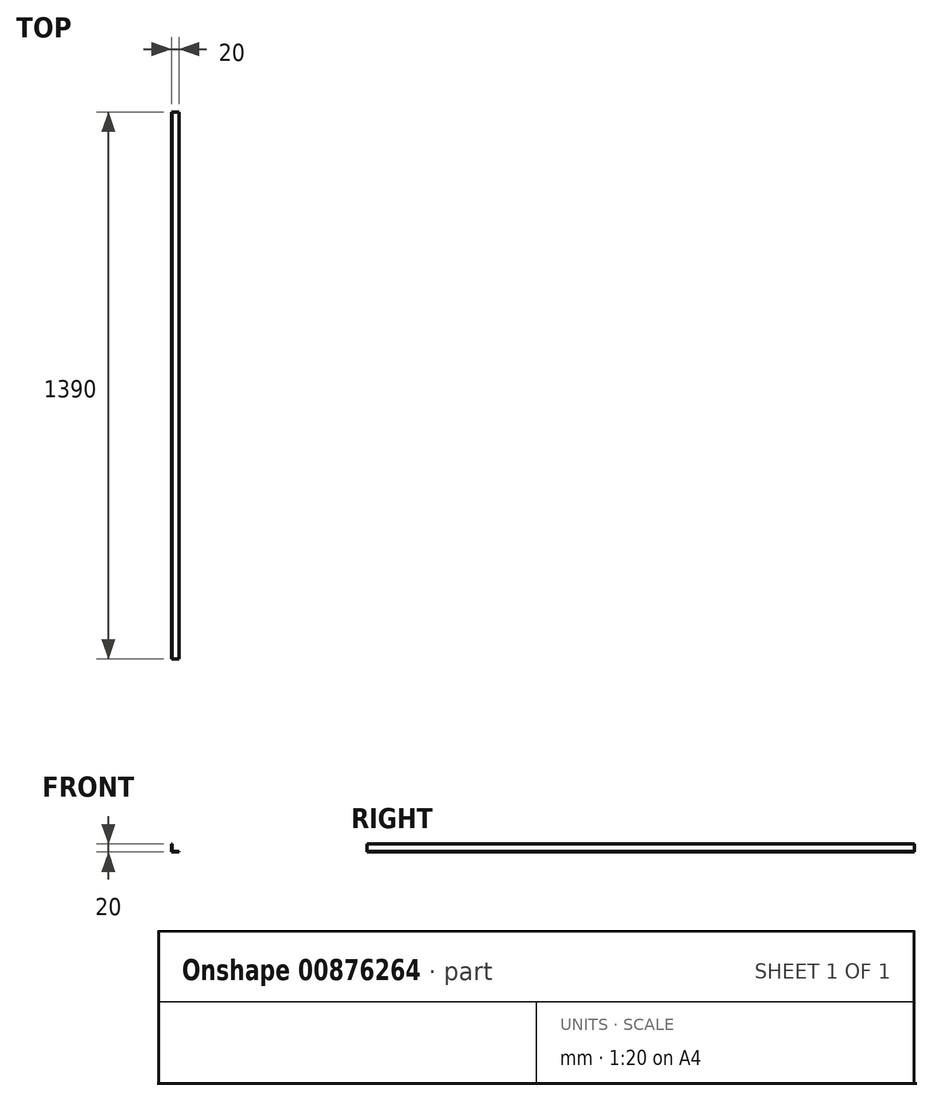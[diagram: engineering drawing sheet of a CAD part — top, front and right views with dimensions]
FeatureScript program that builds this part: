
annotation { "Feature Type Name" : "Feature", "Feature Type Description" : "" }
export const myFeature = defineFeature(function(context is Context, id is Id, definition is map)
    precondition{}
    {
        {
            var Q0;
            Q0=qCreatedBy(makeId("Front.planeOp"),FACE);
            var sketch = newSketch(context, id + "F0", { "sketchPlane" : qUnion([Q0])});
            skLineSegment(sketch, "E0", {"start": v(20, -29.07) * mm, "end": v(20, -27.57) * mm});
            skLineSegment(sketch, "E1", {"start": v(1.5, -9.07) * mm, "end": v(0, -9.07) * mm});
            skLineSegment(sketch, "E2", {"start": v(20, -29.07) * mm, "end": v(0, -29.07) * mm});
            skLineSegment(sketch, "E3", {"start": v(0, -29.07) * mm, "end": v(0, -9.07) * mm});
            skLineSegment(sketch, "E4", {"start": v(20, -27.57) * mm, "end": v(1.5, -27.57) * mm});
            skLineSegment(sketch, "E5", {"start": v(1.5, -27.57) * mm, "end": v(1.5, -9.07) * mm});
            skSolve(sketch);
        }
        {
            var Q0;
            Q0=makeQuery(id+"F0.imprint","IMPRINT",FACE,{"disambiguationData":[TD([[makeQuery(id+"F0.imprint","IMPRINT",EDGE,{"derivedFrom":sQuery(id+"F0.wireOp",EDGE,"E0")}),1.0]])]});
            extrude(context, id + "F1", {"entities" : qUnion([Q0]), "depth" : 1450 * mm - 60 * mm, "offsetDistance" : 25.4 * mm});
        }
    });
